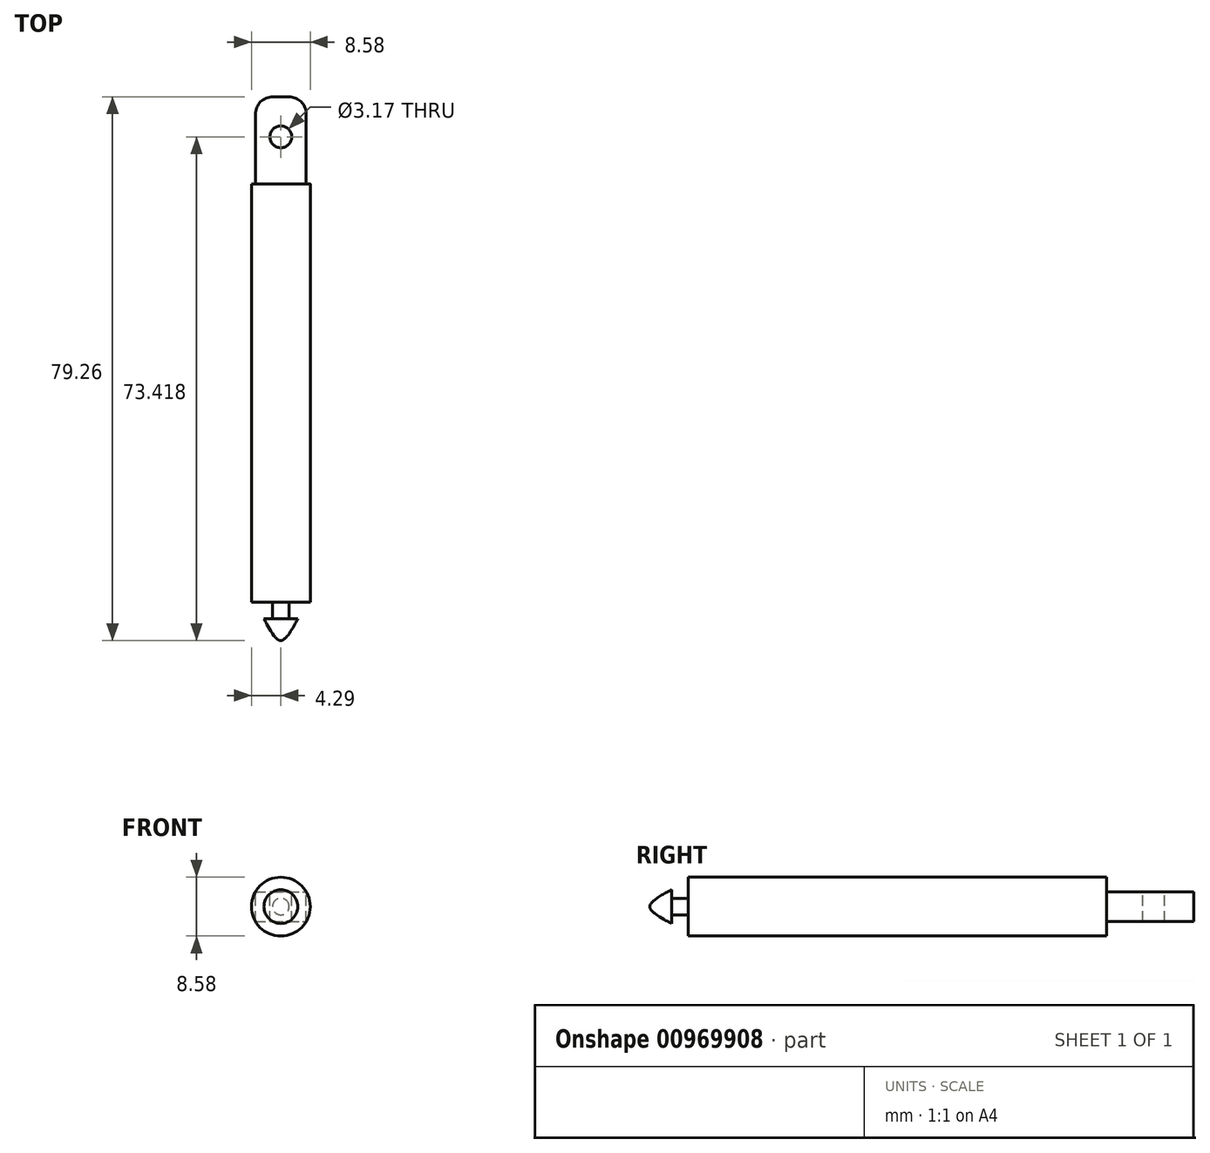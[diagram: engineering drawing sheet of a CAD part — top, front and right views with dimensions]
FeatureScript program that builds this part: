
annotation { "Feature Type Name" : "Feature", "Feature Type Description" : "" }
export const myFeature = defineFeature(function(context is Context, id is Id, definition is map)
    precondition{}
    {
        {
            var Q0;
            Q0=qCreatedBy(makeId("Front.planeOp"),FACE);
            var sketch = newSketch(context, id + "F0", { "sketchPlane" : qUnion([Q0])});
            skCircle(sketch, "E0", {"center": v(0, 0) * mm, "radius": 4.3 * mm});
            skSolve(sketch);
        }
        {
            var Q0;
            Q0=makeQuery(id+"F0.imprint","IMPRINT",FACE,{"disambiguationData":[TD([[makeQuery(id+"F0.imprint","IMPRINT",EDGE,{"derivedFrom":sQuery(id+"F0.wireOp",EDGE,"E0")}),1.0]])]});
            extrude(context, id + "F1", {"entities" : qUnion([Q0]), "oppositeDirection" : true, "depth" : 60.96 * mm, "offsetDistance" : 25.4 * mm});
        }
        {
            var Q0;
            Q0=qCreatedBy(makeId("Front.planeOp"),FACE);
            var sketch = newSketch(context, id + "F2", { "sketchPlane" : qUnion([Q0])});
            skCircle(sketch, "E1", {"center": v(0, 0) * mm, "radius": 1.2 * mm});
            skSolve(sketch);
        }
        {
            var Q0;
            Q0 = qSketchRegion(id + "F2", true);
            extrude(context, id + "F3", {"entities" : qUnion([Q0]), "operationType" : NewBodyOperationType.ADD, "depth" : 2.41 * mm, "offsetDistance" : 25.4 * mm});
        }
        {
            var Q0;
            Q0=qCreatedBy(makeId("Right.planeOp"),FACE);
            var sketch = newSketch(context, id + "F4", { "sketchPlane" : qUnion([Q0])});
            skLineSegment(sketch, "E2", {"start": v(-2.41, 0) * mm, "end": v(-2.41, 2.46) * mm});
            skFitSpline(sketch, "E3", {"points": [v(-2.41, 2.46) * mm, v(-5.59, 0) * mm], "startDerivative": vector(-3.58, -1.66) * mm, "endDerivative": vector(0.5, -1.95) * mm});
            skLineSegment(sketch, "E4", {"start": v(-5.59, 0) * mm, "end": v(-2.41, 0) * mm});
            skSolve(sketch);
        }
        {
            var Q0;
            Q0 = qSketchRegion(id + "F4", true);
            var Q1;
            Q1=sQuery(id+"F4.wireOp",EDGE,"E4");
            revolve(context, id + "F5", {"operationType" : NewBodyOperationType.ADD, "surfaceOperationType" : NewSurfaceOperationType.NEW, "entities" : qUnion([Q0]), "axis" : qUnion([Q1]), "revolveType" : RevolveType.FULL});
        }
        {
            var Q0;
            Q0=makeQuery(id+"F1.opExtrude","CAP_FACE",FACE,{"disambiguationData":[OSD([sQuery(id+"F0.wireOp",EDGE,"E0")])],"isStart":false});
            var sketch = newSketch(context, id + "F6", { "sketchPlane" : qUnion([Q0])});
            skLineSegment(sketch, "E5.bottom", {"start": v(3.7, -2.16) * mm, "end": v(-3.7, -2.16) * mm});
            skLineSegment(sketch, "E5.top", {"start": v(3.7, 2.16) * mm, "end": v(-3.7, 2.16) * mm});
            skLineSegment(sketch, "E5.left", {"start": v(3.7, -2.16) * mm, "end": v(3.7, 2.16) * mm});
            skLineSegment(sketch, "E5.right", {"start": v(-3.7, -2.16) * mm, "end": v(-3.7, 2.16) * mm});
            skPoint(sketch, "E5.middle", {"position": v(0, 0) * mm});
            skSolve(sketch);
        }
        {
            var Q0;
            Q0 = qSketchRegion(id + "F6", true);
            extrude(context, id + "F7", {"entities" : qUnion([Q0]), "operationType" : NewBodyOperationType.ADD, "depth" : 12.7 * mm, "offsetDistance" : 25.4 * mm});
        }
        {
            var Q0;
            Q0=makeQuery(id+"F7.opExtrude","CAP_EDGE",EDGE,{"disambiguationData":[OSD([sQuery(id+"F6.wireOp",EDGE,"E5.left")])],"isStart":false});
            var Q1;
            Q1=makeQuery(id+"F7.opExtrude","CAP_EDGE",EDGE,{"disambiguationData":[OSD([sQuery(id+"F6.wireOp",EDGE,"E5.right")])],"isStart":false});
            fillet(context, id + "F8", {"entities" : qUnion([Q0, Q1]), "radius" : 2.54 * mm, "tangentPropagation" : true, "allowEdgeOverflow" : false});
        }
        {
            var Q0;
            Q0=makeQuery(id+"F7.opExtrude","SWEPT_FACE",FACE,{"disambiguationData":[OSD([sQuery(id+"F6.wireOp",EDGE,"E5.top")])]});
            var sketch = newSketch(context, id + "F9", { "sketchPlane" : qUnion([Q0])});
            skCircle(sketch, "E6", {"center": v(0, 67.82) * mm, "radius": 1.59 * mm});
            skPoint(sketch, "E6.centerSnap0", {"position": v(0, 60.96) * mm});
            skSolve(sketch);
        }
        {
            var Q0;
            Q0 = qSketchRegion(id + "F9", true);
            extrude(context, id + "F10", {"entities" : qUnion([Q0]), "operationType" : NewBodyOperationType.REMOVE, "endBound" : BoundingType.THROUGH_ALL, "oppositeDirection" : true, "depth" : 25.4 * mm, "offsetDistance" : 25.4 * mm});
        }
    });
